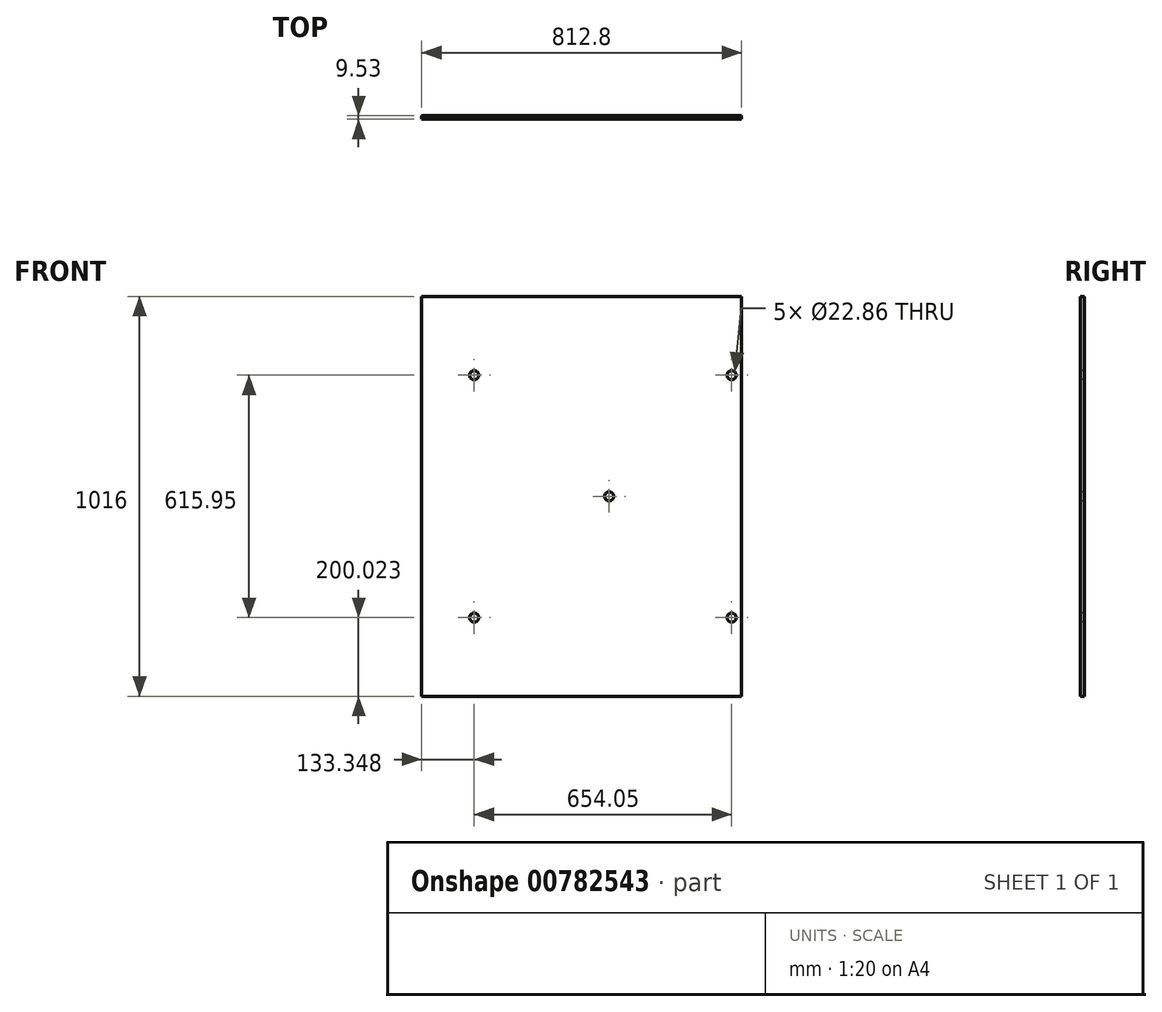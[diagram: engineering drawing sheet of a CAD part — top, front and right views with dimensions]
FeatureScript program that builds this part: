
annotation { "Feature Type Name" : "Feature", "Feature Type Description" : "" }
export const myFeature = defineFeature(function(context is Context, id is Id, definition is map)
    precondition{}
    {
        {
            var Q0;
            Q0=qCreatedBy(makeId("Front.planeOp"),FACE);
            var sketch = newSketch(context, id + "F0", { "sketchPlane" : qUnion([Q0])});
            skLineSegment(sketch, "E0.bottom", {"start": v(-778.91, 985.9) * mm, "end": v(33.89, 985.9) * mm});
            skLineSegment(sketch, "E0.top", {"start": v(-778.91, -30.1) * mm, "end": v(33.89, -30.1) * mm});
            skLineSegment(sketch, "E0.left", {"start": v(-778.91, 985.9) * mm, "end": v(-778.91, -30.1) * mm});
            skLineSegment(sketch, "E0.right", {"start": v(33.89, 985.9) * mm, "end": v(33.89, -30.1) * mm});
            skSolve(sketch);
        }
        {
            var Q0;
            Q0 = qSketchRegion(id + "F0", true);
            extrude(context, id + "F1", {"entities" : qUnion([Q0]), "depth" : 9.52 * mm, "offsetDistance" : 25.4 * mm});
        }
        {
            var Q0;
            Q0=qCreatedBy(makeId("Front.planeOp"),FACE);
            var sketch = newSketch(context, id + "F2", { "sketchPlane" : qUnion([Q0])});
            skPoint(sketch, "E1", {"position": v(-645.56, 785.88) * mm});
            skPoint(sketch, "E2", {"position": v(-645.56, 169.93) * mm});
            skPoint(sketch, "E3", {"position": v(8.49, 785.88) * mm});
            skPoint(sketch, "E4", {"position": v(8.49, 169.93) * mm});
            skPoint(sketch, "E5", {"position": v(-302.66, 477.9) * mm});
            skSolve(sketch);
        }
        {
            var Q0;
            Q0=sQuery(id+"F2.wireOp",VERTEX,"E1");
            var Q1;
            Q1=sQuery(id+"F2.wireOp",VERTEX,"E3");
            var Q2;
            Q2=sQuery(id+"F2.wireOp",VERTEX,"E5");
            var Q3;
            Q3=sQuery(id+"F2.wireOp",VERTEX,"E4");
            var Q4;
            Q4=sQuery(id+"F2.wireOp",VERTEX,"E2");
            var Q5;
            Q5=makeQuery(id+"F1.opExtrude","SWEPT_BODY",BODY,{"disambiguationData":[OSD([sQuery(id+"F0.wireOp",EDGE,"E0.bottom"),sQuery(id+"F0.wireOp",EDGE,"E0.top"),sQuery(id+"F0.wireOp",EDGE,"E0.left"),sQuery(id+"F0.wireOp",EDGE,"E0.right")])]});
            hole(context, id + "F3", {"style" : HoleStyle.SIMPLE, "endStyle" : HoleEndStyle.THROUGH, "oppositeDirection" : true, "holeDiameter" : 22.86 * mm, "majorDiameter" : 6.35 * mm, "isTappedThrough" : true, "tappedDepth" : 12.7 * mm, "tapClearance" : 3, "locations" : qUnion([Q0, Q1, Q2, Q3, Q4]), "scope" : qUnion([Q5]), "startStyle" : HoleStartStyle.PART});
        }
    });
